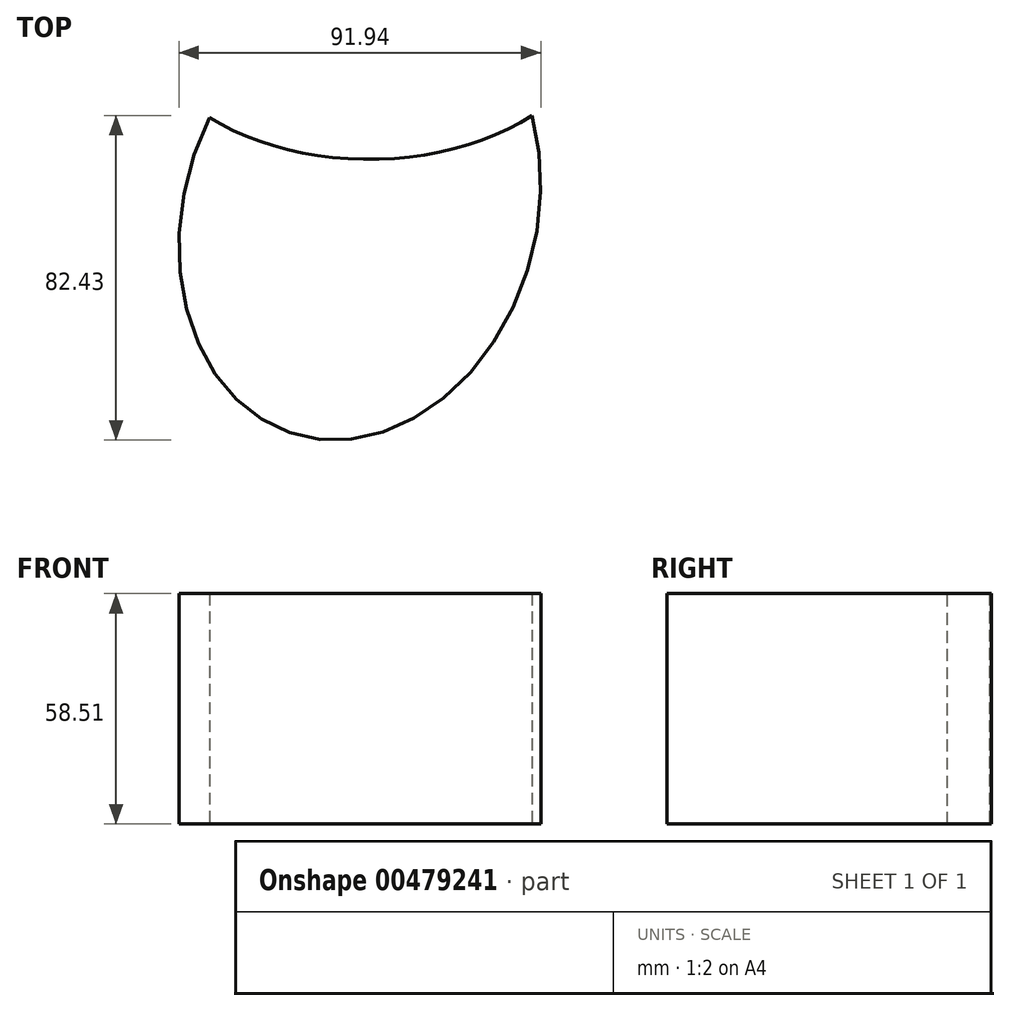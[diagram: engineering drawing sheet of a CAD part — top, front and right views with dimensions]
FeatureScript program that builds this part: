
annotation { "Feature Type Name" : "Feature", "Feature Type Description" : "" }
export const myFeature = defineFeature(function(context is Context, id is Id, definition is map)
    precondition{}
    {
        {
            var Q0;
            Q0=qCreatedBy(makeId("Top.planeOp"),FACE);
            var sketch = newSketch(context, id + "F0", { "sketchPlane" : qUnion([Q0])});
            skEllipse(sketch, "E0", {"center": v(14.25, 0) * mm, "majorRadius": 39.54 * mm, "minorRadius": 59.52 * mm, "majorAxis": v(0, -1)});
            skEllipse(sketch, "E1", {"center": v(11.91, -53.69) * mm, "majorRadius": 58.12 * mm, "minorRadius": 44.8 * mm, "majorAxis": v(0.28, 0.96)});
            skSolve(sketch);
        }
        {
            var Q0;
            {var subQ0=sQuery(id+"F0.wireOp",EDGE,"E1");var subQ1=sQuery(id+"F0.wireOp",EDGE,"E0");var subQ2=makeQuery(id+"F0.imprint","INTERSECT",VERTEX,{"disambiguationData":[OD(0.0)],"derivedFrom":[subQ1,subQ0]});Q0=makeQuery(id+"F0.imprint","IMPRINT",FACE,{"disambiguationData":[TD([[makeQuery(id+"F0.imprint","IMPRINT",EDGE,{"disambiguationData":[TD([[subQ2,-1.0]])],"derivedFrom":subQ1}),-1.0]])]});}
            extrude(context, id + "F1", {"entities" : qUnion([Q0]), "depth" : 58.5 * mm});
        }
    });
